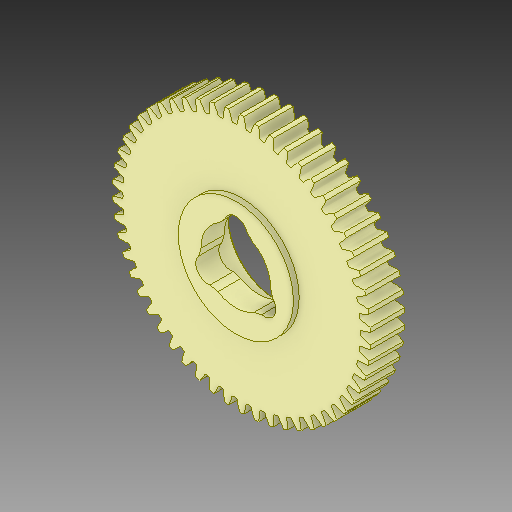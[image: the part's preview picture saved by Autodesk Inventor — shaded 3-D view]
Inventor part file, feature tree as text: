
AUTODESK INVENTOR PART (.ipt)
format: ipt  version: 2017 (Build 210142000, 142)  size: 1,226,240 bytes
history: native  units: in
note: dims shown in document units (in); Inventor stores cm internally (conversion verified against a paired STEP export)
features: chamfer x1
ambient origin geometry x8: Origin, YZ Plane, XZ Plane, XY Plane, X Axis, Y Axis, Z Axis, Center Point
bodies: Solid1 (feature_tree)
feature tree (1):
  chamfer  "Chamfer1"  [1 undecoded]
note: 1 required parameter value undecoded (feature->parameter linkage not recoverable at this tier; creation-order binding heuristic only, values carry confidence <= 0.55)
